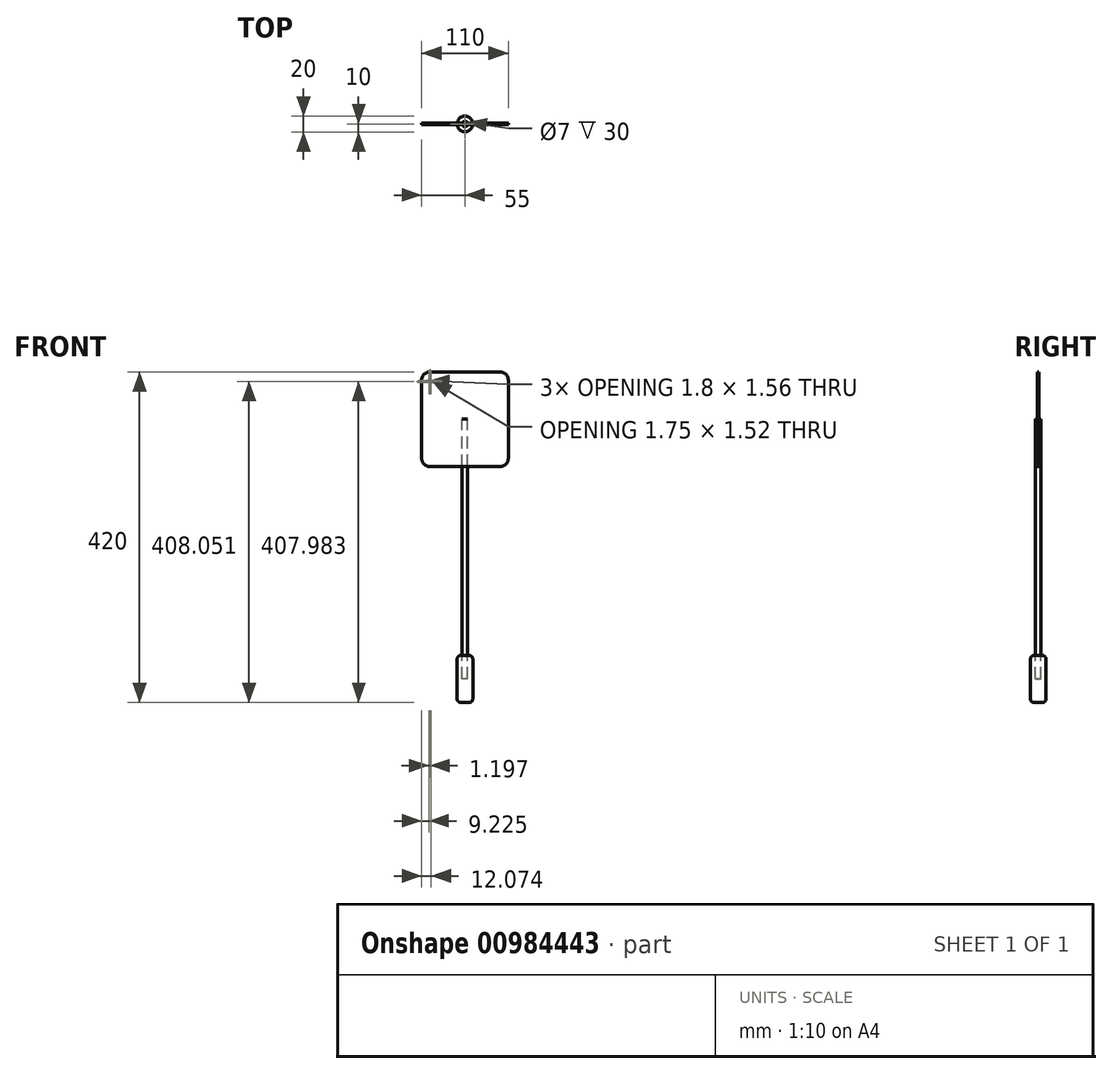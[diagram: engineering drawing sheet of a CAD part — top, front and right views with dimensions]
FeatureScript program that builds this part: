
annotation { "Feature Type Name" : "Feature", "Feature Type Description" : "" }
export const myFeature = defineFeature(function(context is Context, id is Id, definition is map)
    precondition{}
    {
        {
            var Q0;
            Q0=qCreatedBy(makeId("Front.planeOp"),FACE);
            var sketch = newSketch(context, id + "F0", { "sketchPlane" : qUnion([Q0])});
            skLineSegment(sketch, "E0", {"start": v(0, 0) * mm, "end": v(0, 420) * mm, "construction": true});
            skLineSegment(sketch, "E1.bottom", {"start": v(55, 420) * mm, "end": v(-55, 420) * mm});
            skLineSegment(sketch, "E1.top", {"start": v(55, 300) * mm, "end": v(-55, 300) * mm});
            skLineSegment(sketch, "E1.left", {"start": v(55, 420) * mm, "end": v(55, 300) * mm});
            skLineSegment(sketch, "E1.right", {"start": v(-55, 420) * mm, "end": v(-55, 300) * mm});
            skLineSegment(sketch, "E2.bottom", {"start": v(0, 0) * mm, "end": v(10, 0) * mm});
            skLineSegment(sketch, "E2.top", {"start": v(0, 60) * mm, "end": v(10, 60) * mm});
            skLineSegment(sketch, "E2.left", {"start": v(0, 0) * mm, "end": v(0, 60) * mm});
            skLineSegment(sketch, "E2.right", {"start": v(10, 0) * mm, "end": v(10, 60) * mm});
            skPoint(sketch, "E3.firstSnap0", {"position": v(-55, 360) * mm});
            skPoint(sketch, "E3.oppositeSnap0", {"position": v(0, 30) * mm});
            skLineSegment(sketch, "E3.bottom", {"start": v(0, 360) * mm, "end": v(-3.5, 360) * mm});
            skLineSegment(sketch, "E3.top", {"start": v(0, 30) * mm, "end": v(-3.5, 30) * mm});
            skLineSegment(sketch, "E3.left", {"start": v(0, 360) * mm, "end": v(0, 30) * mm});
            skLineSegment(sketch, "E3.right", {"start": v(-3.5, 360) * mm, "end": v(-3.5, 30) * mm});
            skSolve(sketch);
        }
        {
            var Q0;
            {var subQ5=sQuery(id+"F0.wireOp",EDGE,"E3.bottom");Q0=makeQuery(id+"F0.imprint","IMPRINT",FACE,{"disambiguationData":[TD([[makeQuery(id+"F0.imprint","IMPRINT",EDGE,{"derivedFrom":subQ5}),1.0]])]});}
            var Q1;
            {var subQ2=sQuery(id+"F0.wireOp",EDGE,"E3.top");Q1=makeQuery(id+"F0.imprint","IMPRINT",FACE,{"disambiguationData":[TD([[makeQuery(id+"F0.imprint","IMPRINT",EDGE,{"derivedFrom":subQ2}),-1.0]])]});}
            var Q2;
            Q2=sQuery(id+"F0.wireOp",EDGE,"E3.left");
            revolve(context, id + "F1", {"surfaceOperationType" : NewSurfaceOperationType.NEW, "entities" : qUnion([Q0, Q1]), "axis" : qUnion([Q2]), "revolveType" : RevolveType.FULL});
        }
        {
            var Q0;
            Q0=makeQuery(id+"F0.imprint","IMPRINT",FACE,{"disambiguationData":[TD([[makeQuery(id+"F0.imprint","IMPRINT",EDGE,{"derivedFrom":sQuery(id+"F0.wireOp",EDGE,"E2.bottom")}),1.0]])]});
            var Q1;
            Q1=sQuery(id+"F0.wireOp",EDGE,"E2.left");
            revolve(context, id + "F2", {"surfaceOperationType" : NewSurfaceOperationType.NEW, "entities" : qUnion([Q0]), "axis" : qUnion([Q1]), "revolveType" : RevolveType.FULL});
        }
        {
            var Q0;
            Q0=makeQuery(id+"F1.opRevolve","SWEPT_BODY",BODY,{"disambiguationData":[OSD([sQuery(id+"F0.wireOp",EDGE,"E3.bottom"),sQuery(id+"F0.wireOp",EDGE,"E3.top"),sQuery(id+"F0.wireOp",EDGE,"E3.left"),sQuery(id+"F0.wireOp",EDGE,"E3.right")])]});
            var Q1;
            Q1=makeQuery(id+"F2.opRevolve","SWEPT_BODY",BODY,{"disambiguationData":[OSD([sQuery(id+"F0.wireOp",EDGE,"E2.bottom"),sQuery(id+"F0.wireOp",EDGE,"E2.top"),sQuery(id+"F0.wireOp",EDGE,"E2.left"),sQuery(id+"F0.wireOp",EDGE,"E2.right"),sQuery(id+"F0.wireOp",EDGE,"E3.left")])]});
            booleanBodies(context, id + "F3", {"operationType" : BooleanOperationType.SUBTRACTION, "tools" : qUnion([Q0]), "targets" : qUnion([Q1]), "keepTools" : true});
        }
        {
            var Q0;
            Q0=makeQuery(id+"F0.imprint","IMPRINT",FACE,{"disambiguationData":[TD([[makeQuery(id+"F0.imprint","IMPRINT",EDGE,{"derivedFrom":sQuery(id+"F0.wireOp",EDGE,"E1.bottom")}),1.0]])]});
            var Q1;
            {var subQ5=sQuery(id+"F0.wireOp",EDGE,"E3.bottom");Q1=makeQuery(id+"F0.imprint","IMPRINT",FACE,{"disambiguationData":[TD([[makeQuery(id+"F0.imprint","IMPRINT",EDGE,{"derivedFrom":subQ5}),1.0]])]});}
            extrude(context, id + "F4", {"entities" : qUnion([Q0, Q1]), "endBound" : BoundingType.SYMMETRIC, "depth" : 2 * mm, "offsetDistance" : 25 * mm});
        }
        {
            var Q0;
            Q0=makeQuery(id+"F4.opExtrude","SWEPT_EDGE",EDGE,{"disambiguationData":[OSD([sQuery(id+"F0.wireOp",EDGE,"E1.bottom"),sQuery(id+"F0.wireOp",EDGE,"E1.right")])]});
            var Q1;
            Q1=makeQuery(id+"F4.opExtrude","SWEPT_EDGE",EDGE,{"disambiguationData":[OSD([sQuery(id+"F0.wireOp",EDGE,"E1.bottom"),sQuery(id+"F0.wireOp",EDGE,"E1.left")])]});
            var Q2;
            Q2=makeQuery(id+"F4.opExtrude","SWEPT_EDGE",EDGE,{"disambiguationData":[OSD([sQuery(id+"F0.wireOp",EDGE,"E1.top"),sQuery(id+"F0.wireOp",EDGE,"E1.right")])]});
            var Q3;
            Q3=makeQuery(id+"F4.opExtrude","SWEPT_EDGE",EDGE,{"disambiguationData":[OSD([sQuery(id+"F0.wireOp",EDGE,"E1.top"),sQuery(id+"F0.wireOp",EDGE,"E1.left")])]});
            fillet(context, id + "F5", {"entities" : qUnion([Q0, Q1, Q2, Q3]), "radius" : 10 * mm, "tangentPropagation" : true, "allowEdgeOverflow" : false});
        }
        {
            var Q0;
            Q0=makeQuery(id+"F2.opRevolve","SWEPT_EDGE",EDGE,{"disambiguationData":[OSD([sQuery(id+"F0.wireOp",EDGE,"E2.top"),sQuery(id+"F0.wireOp",EDGE,"E2.right")])]});
            var Q1;
            Q1=makeQuery(id+"F2.opRevolve","SWEPT_EDGE",EDGE,{"disambiguationData":[OSD([sQuery(id+"F0.wireOp",EDGE,"E2.bottom"),sQuery(id+"F0.wireOp",EDGE,"E2.right")])]});
            fillet(context, id + "F6", {"entities" : qUnion([Q0, Q1]), "radius" : 5 * mm, "tangentPropagation" : true, "allowEdgeOverflow" : false});
        }
        {
            var Q0;
            Q0=qCreatedBy(makeId("Front.planeOp"),FACE);
            var sketch = newSketch(context, id + "F7", { "sketchPlane" : qUnion([Q0])});
            skLineSegment(sketch, "E4.0.0", {"start": v(-45, 300) * mm, "end": v(45, 300) * mm, "construction": true});
            skArc(sketch, "E4.0.1", {"start": v(45, 300) * mm, "mid": v(52.07, 302.93) * mm, "end": v(55, 310) * mm, "construction": true});
            skLineSegment(sketch, "E4.0.2", {"start": v(55, 310) * mm, "end": v(55, 410) * mm, "construction": true});
            skArc(sketch, "E4.0.3", {"start": v(55, 410) * mm, "mid": v(52.07, 417.07) * mm, "end": v(45, 420) * mm, "construction": true});
            skLineSegment(sketch, "E4.0.4", {"start": v(45, 420) * mm, "end": v(-45, 420) * mm, "construction": true});
            skArc(sketch, "E4.0.5", {"start": v(-45, 420) * mm, "mid": v(-52.07, 417.07) * mm, "end": v(-55, 410) * mm, "construction": true});
            skLineSegment(sketch, "E4.0.6", {"start": v(-55, 410) * mm, "end": v(-55, 310) * mm, "construction": true});
            skArc(sketch, "E4.0.7", {"start": v(-55, 310) * mm, "mid": v(-52.07, 302.93) * mm, "end": v(-45, 300) * mm, "construction": true});
            skLineSegment(sketch, "E5", {"start": v(-45, 410) * mm, "end": v(-43.2, 410) * mm});
            skLineSegment(sketch, "E6", {"start": v(-43.2, 410) * mm, "end": v(-44.1, 408.44) * mm});
            skPoint(sketch, "E6.endSnap0", {"position": v(-44.1, 410) * mm});
            skLineSegment(sketch, "E7", {"start": v(-44.1, 408.44) * mm, "end": v(-45, 410) * mm});
            skLineSegment(sketch, "E8", {"start": v(-42.93, 408.74) * mm, "end": v(-43.8, 407.22) * mm});
            skPoint(sketch, "E8.startSnap0", {"position": v(-43.65, 409.22) * mm});
            skLineSegment(sketch, "E9", {"start": v(-43.8, 407.22) * mm, "end": v(-42.05, 407.22) * mm});
            skLineSegment(sketch, "E10", {"start": v(-42.05, 407.22) * mm, "end": v(-42.93, 408.74) * mm});
            skLineSegment(sketch, "E11", {"start": v(-46.68, 408.83) * mm, "end": v(-44.87, 408.83) * mm});
            skLineSegment(sketch, "E12", {"start": v(-44.88, 408.83) * mm, "end": v(-45.78, 407.27) * mm});
            skPoint(sketch, "E12.endSnap0", {"position": v(-45.78, 408.83) * mm});
            skLineSegment(sketch, "E13", {"start": v(-45.77, 407.27) * mm, "end": v(-46.67, 408.83) * mm});
            skLineSegment(sketch, "E14", {"start": v(-44.58, 407.61) * mm, "end": v(-45.48, 406.05) * mm});
            skPoint(sketch, "E14.startSnap0", {"position": v(-45.33, 408.05) * mm});
            skLineSegment(sketch, "E15", {"start": v(-45.48, 406.05) * mm, "end": v(-43.68, 406.05) * mm});
            skLineSegment(sketch, "E16", {"start": v(-43.68, 406.05) * mm, "end": v(-44.58, 407.61) * mm});
            skLineSegment(sketch, "E17", {"start": v(-44.8, 407.22) * mm, "end": v(-45.44, 407.22) * mm, "construction": true});
            skPoint(sketch, "E18", {"position": v(-43.88, 408.83) * mm});
            skLineSegment(sketch, "E19", {"start": v(-43.88, 408.83) * mm, "end": v(-44.95, 408.83) * mm, "construction": true});
            skSolve(sketch);
        }
        {
            var Q0;
            Q0=makeQuery(id+"F7.imprint","IMPRINT",FACE,{"disambiguationData":[TD([[makeQuery(id+"F7.imprint","IMPRINT",EDGE,{"derivedFrom":sQuery(id+"F7.wireOp",EDGE,"E5")}),-1.0]])]});
            var Q1;
            Q1=makeQuery(id+"F7.imprint","IMPRINT",FACE,{"disambiguationData":[TD([[makeQuery(id+"F7.imprint","IMPRINT",EDGE,{"derivedFrom":sQuery(id+"F7.wireOp",EDGE,"E11")}),-1.0]])]});
            var Q2;
            Q2=makeQuery(id+"F7.imprint","IMPRINT",FACE,{"disambiguationData":[TD([[makeQuery(id+"F7.imprint","IMPRINT",EDGE,{"derivedFrom":sQuery(id+"F7.wireOp",EDGE,"E14")}),1.0]])]});
            var Q3;
            Q3=makeQuery(id+"F7.imprint","IMPRINT",FACE,{"disambiguationData":[TD([[makeQuery(id+"F7.imprint","IMPRINT",EDGE,{"derivedFrom":sQuery(id+"F7.wireOp",EDGE,"E8")}),1.0]])]});
            var Q4;
            Q4=makeQuery(id+"F4.opExtrude","CAP_FACE",FACE,{"disambiguationData":[OSD([sQuery(id+"F0.wireOp",EDGE,"E1.bottom"),sQuery(id+"F0.wireOp",EDGE,"E1.top"),sQuery(id+"F0.wireOp",EDGE,"E1.left"),sQuery(id+"F0.wireOp",EDGE,"E1.right")])],"isStart":true});
            extrude(context, id + "F8", {"entities" : qUnion([Q0, Q1, Q2, Q3]), "operationType" : NewBodyOperationType.REMOVE, "endBound" : BoundingType.SYMMETRIC, "oppositeDirection" : true, "depth" : 25 * mm, "endBoundEntityFace" : qUnion([Q4]), "offsetDistance" : 25 * mm});
        }
    });
